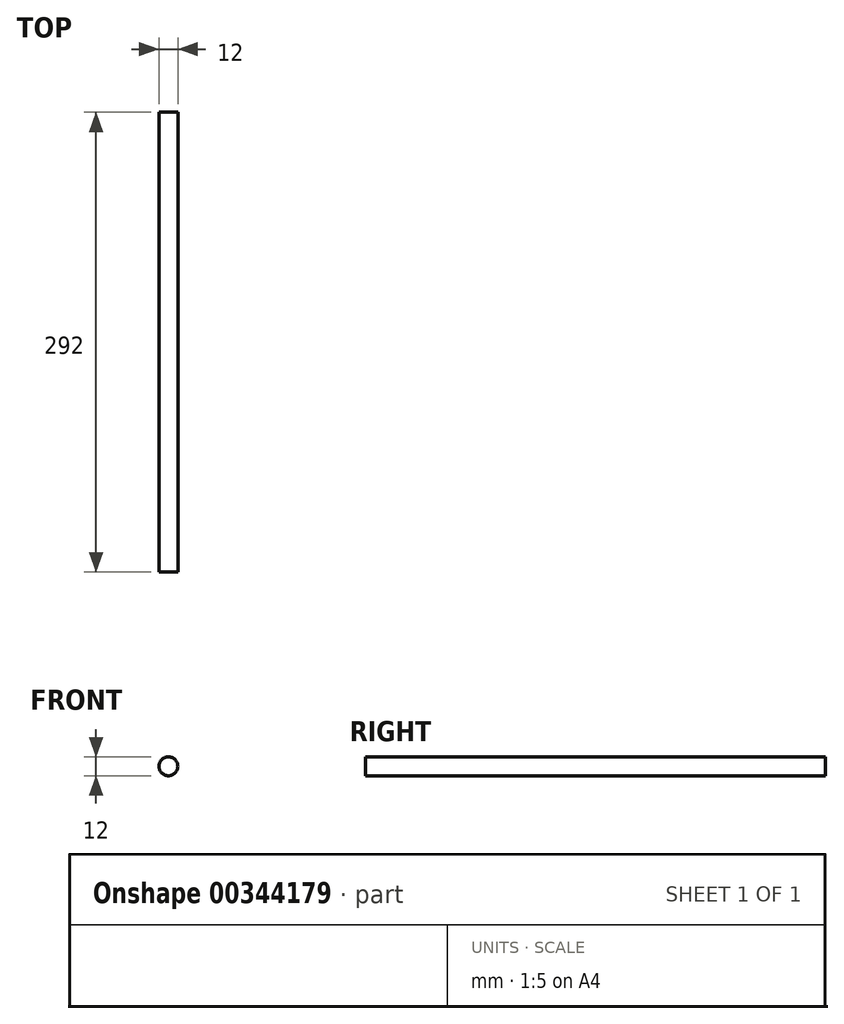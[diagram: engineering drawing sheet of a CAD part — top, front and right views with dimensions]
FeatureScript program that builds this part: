
annotation { "Feature Type Name" : "Feature", "Feature Type Description" : "" }
export const myFeature = defineFeature(function(context is Context, id is Id, definition is map)
    precondition{}
    {
        {
            var Q0;
            Q0=qCreatedBy(makeId("Front.planeOp"),FACE);
            var sketch = newSketch(context, id + "F0", { "sketchPlane" : qUnion([Q0])});
            skCircle(sketch, "E0", {"center": v(0, 0) * mm, "radius": 6 * mm});
            skSolve(sketch);
        }
        {
            var Q0;
            Q0 = qSketchRegion(id + "F0", true);
            extrude(context, id + "F1", {"entities" : qUnion([Q0]), "oppositeDirection" : true, "depth" : 292 * mm});
        }
    });
